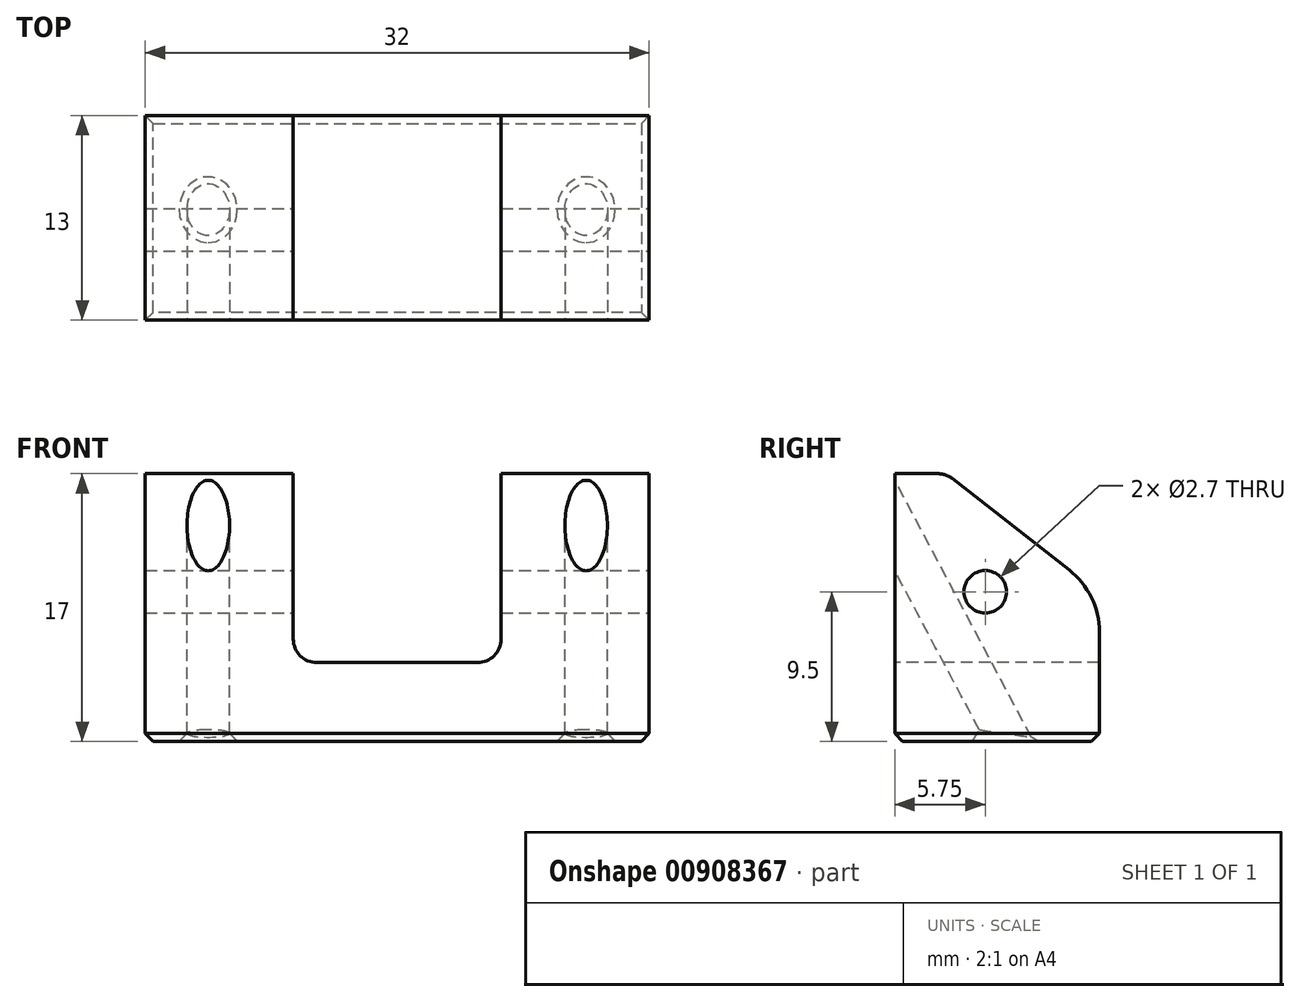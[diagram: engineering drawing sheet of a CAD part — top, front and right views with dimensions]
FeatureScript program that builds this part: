
annotation { "Feature Type Name" : "Feature", "Feature Type Description" : "" }
export const myFeature = defineFeature(function(context is Context, id is Id, definition is map)
    precondition{}
    {
        {
            var Q0;
            Q0=qCreatedBy(makeId("Right.planeOp"),FACE);
            var sketch = newSketch(context, id + "F0", { "sketchPlane" : qUnion([Q0])});
            skLineSegment(sketch, "E0", {"start": v(0, 0) * mm, "end": v(0, 17) * mm});
            skLineSegment(sketch, "E1", {"start": v(0, 17) * mm, "end": v(-13, 17) * mm});
            skLineSegment(sketch, "E2", {"start": v(-13, 17) * mm, "end": v(-13, 7.62) * mm});
            skLineSegment(sketch, "E3", {"start": v(-13, 7.62) * mm, "end": v(-3.25, 0) * mm});
            skLineSegment(sketch, "E4", {"start": v(-3.25, 0) * mm, "end": v(0, 0) * mm});
            skSolve(sketch);
        }
        {
            var Q0;
            Q0 = qSketchRegion(id + "F0", true);
            extrude(context, id + "F1", {"entities" : qUnion([Q0]), "endBound" : BoundingType.SYMMETRIC, "depth" : 32 * mm, "offsetDistance" : 25 * mm});
        }
        {
            var Q0;
            Q0=makeQuery(id+"F1.opExtrude","SWEPT_FACE",FACE,{"disambiguationData":[OSD([sQuery(id+"F0.wireOp",EDGE,"E0")])]});
            var sketch = newSketch(context, id + "F2", { "sketchPlane" : qUnion([Q0])});
            skLineSegment(sketch, "E5.bottom", {"start": v(6.6, 12) * mm, "end": v(-6.6, 12) * mm});
            skLineSegment(sketch, "E5.top", {"start": v(6.6, -12) * mm, "end": v(-6.6, -12) * mm});
            skLineSegment(sketch, "E5.left", {"start": v(6.6, 12) * mm, "end": v(6.6, -12) * mm});
            skLineSegment(sketch, "E5.right", {"start": v(-6.6, 12) * mm, "end": v(-6.6, -12) * mm});
            skPoint(sketch, "E5.middle", {"position": v(0, 0) * mm});
            skSolve(sketch);
        }
        {
            var Q0;
            Q0 = qSketchRegion(id + "F2", true);
            extrude(context, id + "F3", {"entities" : qUnion([Q0]), "operationType" : NewBodyOperationType.REMOVE, "endBound" : BoundingType.THROUGH_ALL, "oppositeDirection" : true, "depth" : 25 * mm, "offsetDistance" : 25 * mm});
        }
        {
            var Q0;
            Q0=makeQuery(id+"F1.opExtrude","CAP_FACE",FACE,{"disambiguationData":[OSD([sQuery(id+"F0.wireOp",EDGE,"E0"),sQuery(id+"F0.wireOp",EDGE,"E1"),sQuery(id+"F0.wireOp",EDGE,"E2"),sQuery(id+"F0.wireOp",EDGE,"E3"),sQuery(id+"F0.wireOp",EDGE,"E4")])],"isStart":false});
            var sketch = newSketch(context, id + "F4", { "sketchPlane" : qUnion([Q0])});
            skPoint(sketch, "E6", {"position": v(-5.75, 7.5) * mm});
            skLineSegment(sketch, "E7", {"start": v(-3.25, 0) * mm, "end": v(-3.25, 17) * mm, "construction": true});
            skSolve(sketch);
        }
        {
            var Q0;
            Q0=sQuery(id+"F4.wireOp",VERTEX,"E6");
            var Q1;
            Q1=makeQuery(id+"F1.opExtrude","SWEPT_BODY",BODY,{"disambiguationData":[OSD([sQuery(id+"F0.wireOp",EDGE,"E0"),sQuery(id+"F0.wireOp",EDGE,"E1"),sQuery(id+"F0.wireOp",EDGE,"E2"),sQuery(id+"F0.wireOp",EDGE,"E3"),sQuery(id+"F0.wireOp",EDGE,"E4")])]});
            hole(context, id + "F5", {"style" : HoleStyle.SIMPLE, "endStyle" : HoleEndStyle.THROUGH, "standardTappedOrClearance" : lookupTablePath({ "standard" : "ISO", "engagement" : "50%", "pitch" : "0.5 mm", "size" : "M3", "type" : "Tapped" }), "standardBlindInLast" : lookupTablePath({ "standard" : "ISO", "engagement" : "50%", "pitch" : "0.5 mm", "size" : "M3", "type" : "Tapped" }), "holeDiameter" : 2.7 * mm, "majorDiameter" : 3 * mm, "showTappedDepth" : true, "isTappedThrough" : true, "tappedDepth" : 98.5 * mm, "tapClearance" : 3, "locations" : qUnion([Q0]), "scope" : qUnion([Q1])});
        }
        {
            var Q0;
            {var subQ2=sQuery(id+"F0.wireOp",EDGE,"E4");Q0=makeQuery(id+"F3.boolean.opBoolean","SPLIT",FACE,{"disambiguationData":[TD([makeQuery(id+"F3.opExtrude","SWEPT_FACE",FACE,{"disambiguationData":[OSD([sQuery(id+"F2.wireOp",EDGE,"E5.right")])]})])],"derivedFrom":makeQuery(id+"F1.opExtrude","SWEPT_FACE",FACE,{"disambiguationData":[OSD([subQ2])]})});}
            var sketch = newSketch(context, id + "F6", { "sketchPlane" : qUnion([Q0])});
            skLineSegment(sketch, "E8", {"start": v(16, -1.75) * mm, "end": v(-16, -1.75) * mm, "construction": true});
            skSolve(sketch);
        }
        {
            var Q0;
            Q0=sQuery(id+"F6.wireOp",EDGE,"E8");
            cPlane(context, id + "F7", {"entities" : qUnion([Q0]), "cplaneType" : CPlaneType.LINE_ANGLE, "offset" : 25 * mm, "angle" : 62 * degree, "width" : 150 * mm, "height" : 150 * mm});
        }
        {
            var Q0;
            Q0=qCreatedBy(id+"F7.planeOp",FACE);
            var sketch = newSketch(context, id + "F8", { "sketchPlane" : qUnion([Q0])});
            skLineSegment(sketch, "E9.0", {"start": v(16, 1.55) * mm, "end": v(6.6, 1.55) * mm, "construction": true});
            skPoint(sketch, "E10", {"position": v(12, 1.55) * mm});
            skPoint(sketch, "E11", {"position": v(-12, 1.55) * mm});
            skLineSegment(sketch, "E12.trimOffspring", {"start": v(-6.6, 1.55) * mm, "end": v(-16, 1.55) * mm, "construction": true});
            skLineSegment(sketch, "E13", {"start": v(12, 1.55) * mm, "end": v(0, 0) * mm, "construction": true});
            skLineSegment(sketch, "E14", {"start": v(0, 0) * mm, "end": v(-12, 1.55) * mm, "construction": true});
            skSolve(sketch);
        }
        {
            var Q0;
            Q0=sQuery(id+"F8.wireOp",VERTEX,"E10");
            var Q1;
            Q1=sQuery(id+"F8.wireOp",VERTEX,"E11");
            var Q2;
            Q2=makeQuery(id+"F1.opExtrude","SWEPT_BODY",BODY,{"disambiguationData":[OSD([sQuery(id+"F0.wireOp",EDGE,"E0"),sQuery(id+"F0.wireOp",EDGE,"E1"),sQuery(id+"F0.wireOp",EDGE,"E2"),sQuery(id+"F0.wireOp",EDGE,"E3"),sQuery(id+"F0.wireOp",EDGE,"E4")])]});
            hole(context, id + "F9", {"style" : HoleStyle.SIMPLE, "endStyle" : HoleEndStyle.THROUGH, "oppositeDirection" : true, "standardTappedOrClearance" : lookupTablePath({ "standard" : "ISO", "engagement" : "50%", "pitch" : "0.5 mm", "size" : "M3", "type" : "Tapped" }), "standardBlindInLast" : lookupTablePath({ "standard" : "ISO", "engagement" : "50%", "pitch" : "0.5 mm", "size" : "M3", "type" : "Tapped" }), "holeDiameter" : 2.7 * mm, "majorDiameter" : 3 * mm, "showTappedDepth" : true, "isTappedThrough" : true, "tappedDepth" : 98.5 * mm, "tapClearance" : 3, "locations" : qUnion([Q0, Q1]), "scope" : qUnion([Q2])});
        }
        {
            var Q0;
            Q0=makeQuery(id+"F1.opExtrude","SWEPT_BODY",BODY,{"disambiguationData":[OSD([sQuery(id+"F0.wireOp",EDGE,"E0"),sQuery(id+"F0.wireOp",EDGE,"E1"),sQuery(id+"F0.wireOp",EDGE,"E2"),sQuery(id+"F0.wireOp",EDGE,"E3"),sQuery(id+"F0.wireOp",EDGE,"E4")])]});
            var Q1;
            {var subQ0=sQuery(id+"F0.wireOp",EDGE,"E0");var subQ1=sQuery(id+"F0.wireOp",EDGE,"E4");Q1=makeQuery(id+"F3.boolean.opBoolean","SPLIT",EDGE,{"disambiguationData":[TD([makeQuery(id+"F3.opExtrude","SWEPT_FACE",FACE,{"disambiguationData":[OSD([sQuery(id+"F2.wireOp",EDGE,"E5.right")])]})])],"derivedFrom":makeQuery(id+"F1.opExtrude","SWEPT_EDGE",EDGE,{"disambiguationData":[OSD([subQ0,subQ1])]})});}
            transform(context, id + "F10", {"entities" : qUnion([Q0]), "transformType" : TransformType.ROTATION, "transformAxis" : qUnion([Q1]), "angle" : 180 * degree, "makeCopy" : false});
        }
        {
            var Q0;
            Q0=makeQuery(id+"F1.opExtrude","SWEPT_BODY",BODY,{"disambiguationData":[OSD([sQuery(id+"F0.wireOp",EDGE,"E0"),sQuery(id+"F0.wireOp",EDGE,"E1"),sQuery(id+"F0.wireOp",EDGE,"E2"),sQuery(id+"F0.wireOp",EDGE,"E3"),sQuery(id+"F0.wireOp",EDGE,"E4")])]});
            var Q1;
            Q1=makeQuery(id+"F1.opExtrude","CAP_EDGE",EDGE,{"disambiguationData":[OSD([sQuery(id+"F0.wireOp",EDGE,"E0")])],"isStart":true});
            transform(context, id + "F11", {"entities" : qUnion([Q0]), "transformType" : TransformType.TRANSLATION_ENTITY, "oppositeDirectionEntity" : true, "transformLine" : qUnion([Q1]), "makeCopy" : false});
        }
        {
            var Q0;
            Q0=makeQuery(id+"F1.opExtrude","SWEPT_FACE",FACE,{"disambiguationData":[OSD([sQuery(id+"F0.wireOp",EDGE,"E1")])]});
            var Q1;
            Q1=makeQuery(id+"F5.hole-0.boolean.opBoolean","COPY",EDGE,{"derivedFrom":makeQuery(id+"F5.hole-0.opRevolve","SWEPT_EDGE",EDGE,{"disambiguationData":[OSD([sQuery(id+"F5.hole-0.sketch.wireOp",EDGE,"core_line_2"),sQuery(id+"F5.hole-0.sketch.wireOp",EDGE,"core_line_3")])]})});
            var Q2;
            Q2=makeQuery(id+"F5.hole-0.boolean.opBoolean","INTERSECT",EDGE,{"derivedFrom":[makeQuery(id+"F1.opExtrude","CAP_FACE",FACE,{"disambiguationData":[OSD([sQuery(id+"F0.wireOp",EDGE,"E0"),sQuery(id+"F0.wireOp",EDGE,"E1"),sQuery(id+"F0.wireOp",EDGE,"E2"),sQuery(id+"F0.wireOp",EDGE,"E3"),sQuery(id+"F0.wireOp",EDGE,"E4")])],"isStart":true}),makeQuery(id+"F5.hole-0.opRevolve","SWEPT_FACE",FACE,{"disambiguationData":[OSD([sQuery(id+"F5.hole-0.sketch.wireOp",EDGE,"core_line_2")])]})]});
            var Q3;
            Q3=makeQuery(id+"F9.hole-1.boolean.opBoolean","INTERSECT",EDGE,{"derivedFrom":[makeQuery(id+"F1.opExtrude","SWEPT_FACE",FACE,{"disambiguationData":[OSD([sQuery(id+"F0.wireOp",EDGE,"E0")])]}),makeQuery(id+"F9.hole-1.opRevolve","SWEPT_FACE",FACE,{"disambiguationData":[OSD([sQuery(id+"F9.hole-1.sketch.wireOp",EDGE,"core_line_2")])]})]});
            var Q4;
            Q4=makeQuery(id+"F9.hole-0.boolean.opBoolean","INTERSECT",EDGE,{"derivedFrom":[makeQuery(id+"F1.opExtrude","SWEPT_FACE",FACE,{"disambiguationData":[OSD([sQuery(id+"F0.wireOp",EDGE,"E0")])]}),makeQuery(id+"F9.hole-0.opRevolve","SWEPT_FACE",FACE,{"disambiguationData":[OSD([sQuery(id+"F9.hole-0.sketch.wireOp",EDGE,"core_line_2")])]})]});
            chamfer(context, id + "F12", {"entities" : qUnion([Q0, Q1, Q2, Q3, Q4]), "width" : 0.5 * mm, "tangentPropagation" : true});
        }
        {
            var Q0;
            {var subQ0=sQuery(id+"F0.wireOp",EDGE,"E3");var subQ1=sQuery(id+"F0.wireOp",EDGE,"E2");Q0=makeQuery(id+"F3.boolean.opBoolean","SPLIT",EDGE,{"disambiguationData":[TD([makeQuery(id+"F3.opExtrude","SWEPT_FACE",FACE,{"disambiguationData":[OSD([sQuery(id+"F2.wireOp",EDGE,"E5.right")])]})])],"derivedFrom":makeQuery(id+"F1.opExtrude","SWEPT_EDGE",EDGE,{"disambiguationData":[OSD([subQ1,subQ0])]})});}
            var Q1;
            {var subQ0=sQuery(id+"F0.wireOp",EDGE,"E3");var subQ1=sQuery(id+"F0.wireOp",EDGE,"E2");Q1=makeQuery(id+"F3.boolean.opBoolean","SPLIT",EDGE,{"disambiguationData":[TD([makeQuery(id+"F3.opExtrude","SWEPT_FACE",FACE,{"disambiguationData":[OSD([sQuery(id+"F2.wireOp",EDGE,"E5.left")])]})])],"derivedFrom":makeQuery(id+"F1.opExtrude","SWEPT_EDGE",EDGE,{"disambiguationData":[OSD([subQ1,subQ0])]})});}
            fillet(context, id + "F13", {"entities" : qUnion([Q0, Q1]), "radius" : 5 * mm, "tangentPropagation" : true, "allowEdgeOverflow" : false});
        }
        {
            var Q0;
            Q0=makeQuery(id+"F3.boolean.opBoolean","COPY",EDGE,{"derivedFrom":makeQuery(id+"F3.opExtrude","SWEPT_EDGE",EDGE,{"disambiguationData":[OSD([sQuery(id+"F2.wireOp",EDGE,"E5.bottom"),sQuery(id+"F2.wireOp",EDGE,"E5.right")])]})});
            var Q1;
            Q1=makeQuery(id+"F3.boolean.opBoolean","COPY",EDGE,{"derivedFrom":makeQuery(id+"F3.opExtrude","SWEPT_EDGE",EDGE,{"disambiguationData":[OSD([sQuery(id+"F2.wireOp",EDGE,"E5.bottom"),sQuery(id+"F2.wireOp",EDGE,"E5.left")])]})});
            var Q2;
            {var subQ0=sQuery(id+"F0.wireOp",EDGE,"E4");var subQ1=sQuery(id+"F0.wireOp",EDGE,"E3");Q2=makeQuery(id+"F3.boolean.opBoolean","SPLIT",EDGE,{"disambiguationData":[TD([makeQuery(id+"F3.opExtrude","SWEPT_FACE",FACE,{"disambiguationData":[OSD([sQuery(id+"F2.wireOp",EDGE,"E5.right")])]})])],"derivedFrom":makeQuery(id+"F1.opExtrude","SWEPT_EDGE",EDGE,{"disambiguationData":[OSD([subQ1,subQ0])]})});}
            var Q3;
            {var subQ0=sQuery(id+"F0.wireOp",EDGE,"E4");var subQ1=sQuery(id+"F0.wireOp",EDGE,"E3");Q3=makeQuery(id+"F3.boolean.opBoolean","SPLIT",EDGE,{"disambiguationData":[TD([makeQuery(id+"F3.opExtrude","SWEPT_FACE",FACE,{"disambiguationData":[OSD([sQuery(id+"F2.wireOp",EDGE,"E5.left")])]})])],"derivedFrom":makeQuery(id+"F1.opExtrude","SWEPT_EDGE",EDGE,{"disambiguationData":[OSD([subQ1,subQ0])]})});}
            fillet(context, id + "F14", {"entities" : qUnion([Q0, Q1, Q2, Q3]), "radius" : 1.5 * mm, "tangentPropagation" : true, "allowEdgeOverflow" : false});
        }
    });
